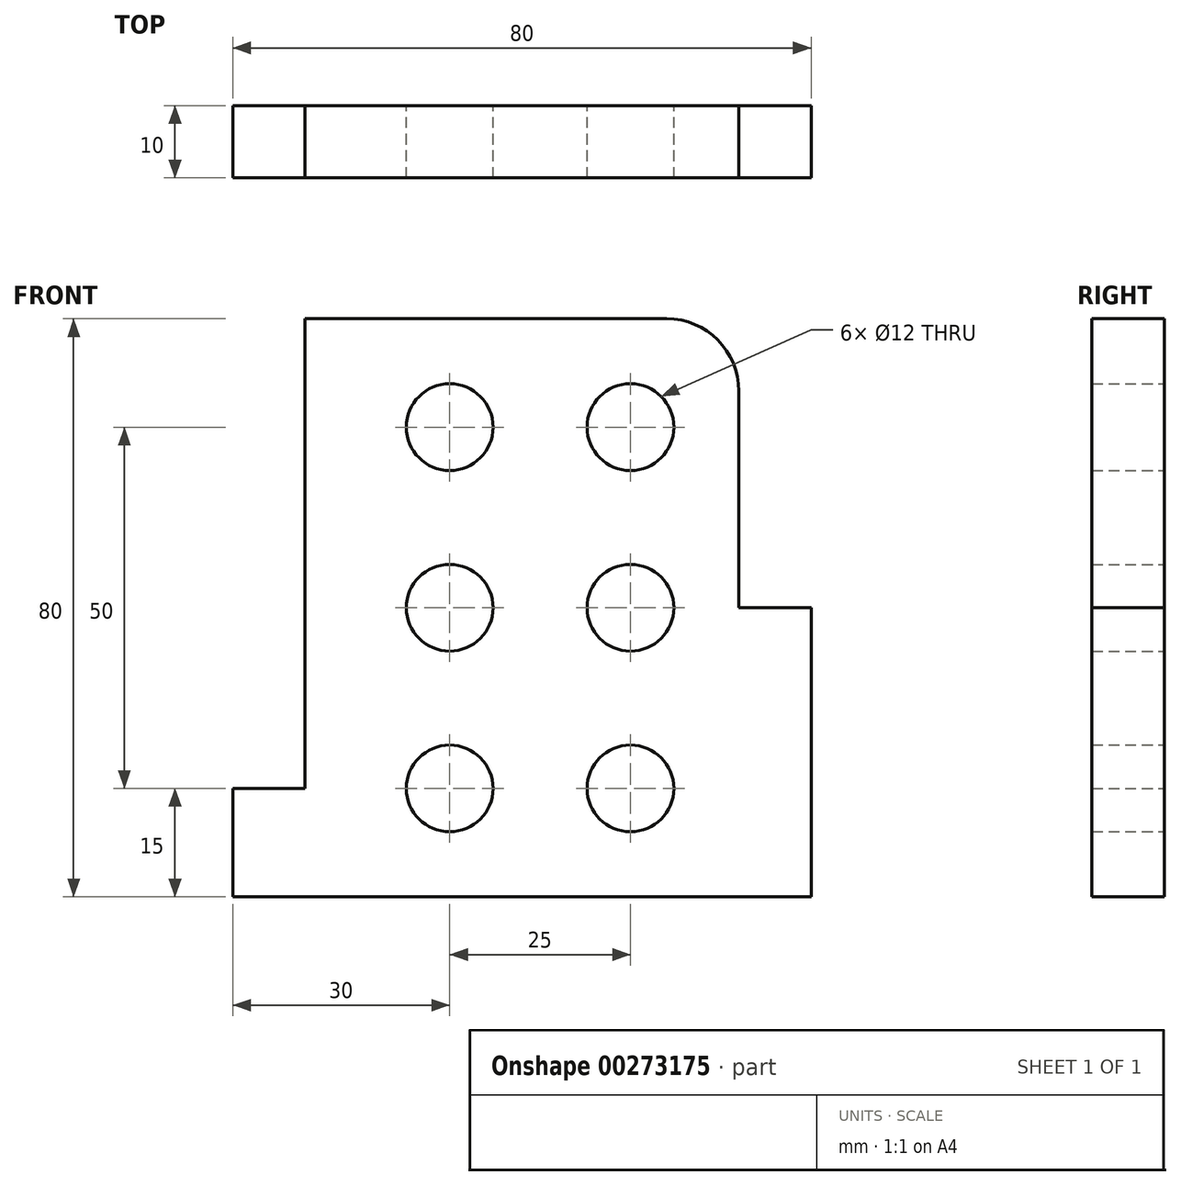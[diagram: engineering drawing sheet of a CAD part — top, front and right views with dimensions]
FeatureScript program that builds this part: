
annotation { "Feature Type Name" : "Feature", "Feature Type Description" : "" }
export const myFeature = defineFeature(function(context is Context, id is Id, definition is map)
    precondition{}
    {
        {
            var Q0;
            Q0=qCreatedBy(makeId("Front.planeOp"),FACE);
            var sketch = newSketch(context, id + "F0", { "sketchPlane" : qUnion([Q0])});
            skLineSegment(sketch, "E0", {"start": v(0, 0) * mm, "end": v(80, 0) * mm});
            skLineSegment(sketch, "E1", {"start": v(0, 0) * mm, "end": v(0, 15) * mm});
            skLineSegment(sketch, "E2", {"start": v(0, 15) * mm, "end": v(10, 15) * mm});
            skLineSegment(sketch, "E3", {"start": v(10, 15) * mm, "end": v(10, 80) * mm});
            skLineSegment(sketch, "E4", {"start": v(80, 0) * mm, "end": v(80, 40) * mm});
            skLineSegment(sketch, "E5", {"start": v(80, 40) * mm, "end": v(70, 40) * mm});
            skLineSegment(sketch, "E6", {"start": v(70, 40) * mm, "end": v(70, 70) * mm});
            skLineSegment(sketch, "E7", {"start": v(10, 80) * mm, "end": v(60, 80) * mm});
            skArc(sketch, "E8", {"start": v(60, 80) * mm, "mid": v(67.07, 77.07) * mm, "end": v(70, 70) * mm});
            skLineSegment(sketch, "E9.bottom", {"start": v(30, 65) * mm, "end": v(55, 65) * mm, "construction": true});
            skLineSegment(sketch, "E9.top", {"start": v(30, 15) * mm, "end": v(55, 15) * mm, "construction": true});
            skLineSegment(sketch, "E9.left", {"start": v(30, 65) * mm, "end": v(30, 15) * mm, "construction": true});
            skLineSegment(sketch, "E9.right", {"start": v(55, 65) * mm, "end": v(55, 15) * mm, "construction": true});
            skPoint(sketch, "E9.middle", {"position": v(42.5, 40) * mm});
            skLineSegment(sketch, "E10", {"start": v(30, 40) * mm, "end": v(55, 40) * mm, "construction": true});
            skCircle(sketch, "E11", {"center": v(30, 65) * mm, "radius": 6 * mm});
            skCircle(sketch, "E12", {"center": v(55, 65) * mm, "radius": 6 * mm});
            skCircle(sketch, "E13", {"center": v(30, 40) * mm, "radius": 6 * mm});
            skCircle(sketch, "E14", {"center": v(55, 40) * mm, "radius": 6 * mm});
            skCircle(sketch, "E15", {"center": v(30, 15) * mm, "radius": 6 * mm});
            skCircle(sketch, "E16", {"center": v(55, 15) * mm, "radius": 6 * mm});
            skSolve(sketch);
        }
        {
            var Q0;
            Q0 = qSketchRegion(id + "F0", true);
            extrude(context, id + "F1", {"entities" : qUnion([Q0]), "depth" : 10 * mm});
        }
    });
